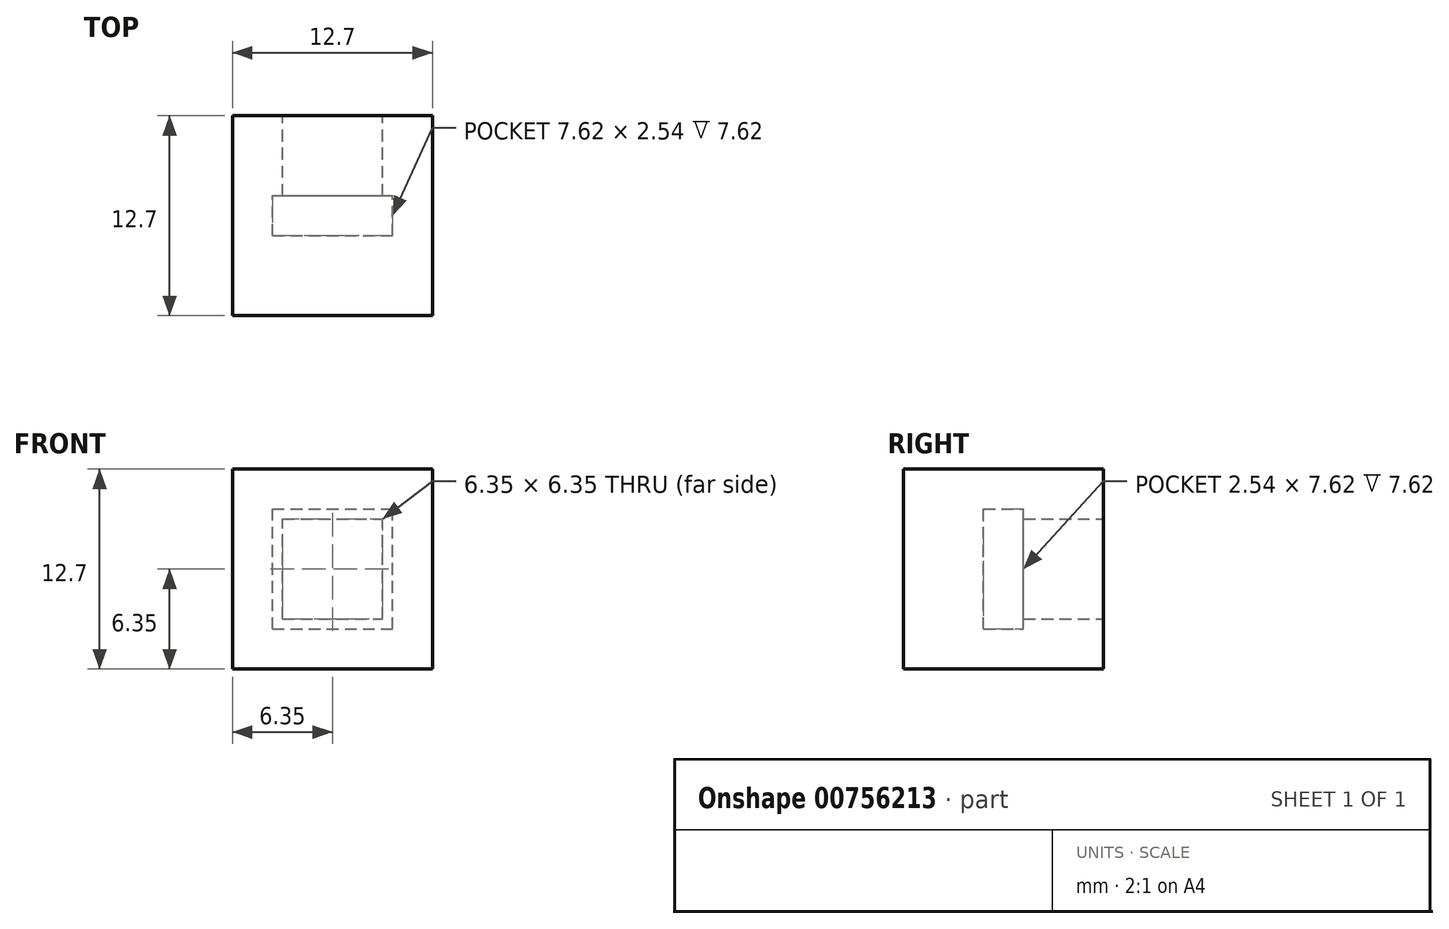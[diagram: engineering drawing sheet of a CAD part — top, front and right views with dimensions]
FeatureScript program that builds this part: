
annotation { "Feature Type Name" : "Feature", "Feature Type Description" : "" }
export const myFeature = defineFeature(function(context is Context, id is Id, definition is map)
    precondition{}
    {
        {
            var Q0;
            Q0=qCreatedBy(makeId("Front.planeOp"),FACE);
            var sketch = newSketch(context, id + "F0", { "sketchPlane" : qUnion([Q0])});
            skLineSegment(sketch, "E0.bottom", {"start": v(-6.35, -6.35) * mm, "end": v(6.35, -6.35) * mm});
            skLineSegment(sketch, "E0.top", {"start": v(-6.35, 6.35) * mm, "end": v(6.35, 6.35) * mm});
            skLineSegment(sketch, "E0.left", {"start": v(-6.35, -6.35) * mm, "end": v(-6.35, 6.35) * mm});
            skLineSegment(sketch, "E0.right", {"start": v(6.35, -6.35) * mm, "end": v(6.35, 6.35) * mm});
            skPoint(sketch, "E0.middle", {"position": v(0, 0) * mm});
            skLineSegment(sketch, "E1.bottom", {"start": v(-3.8, -3.81) * mm, "end": v(3.81, -3.81) * mm});
            skLineSegment(sketch, "E1.top", {"start": v(-3.81, 3.81) * mm, "end": v(3.8, 3.81) * mm});
            skLineSegment(sketch, "E1.left", {"start": v(-3.8, -3.81) * mm, "end": v(-3.81, 3.8) * mm});
            skLineSegment(sketch, "E1.right", {"start": v(3.81, -3.81) * mm, "end": v(3.8, 3.81) * mm});
            skLineSegment(sketch, "E2.bottom", {"start": v(-3.17, -3.18) * mm, "end": v(3.18, -3.18) * mm});
            skLineSegment(sketch, "E2.top", {"start": v(-3.18, 3.18) * mm, "end": v(3.17, 3.18) * mm});
            skLineSegment(sketch, "E2.left", {"start": v(-3.17, -3.18) * mm, "end": v(-3.18, 3.18) * mm});
            skLineSegment(sketch, "E2.right", {"start": v(3.18, -3.18) * mm, "end": v(3.17, 3.18) * mm});
            skSolve(sketch);
        }
        {
            var Q0;
            Q0 = qSketchRegion(id + "F0", true);
            var Q1;
            Q1=makeQuery(id+"F0.imprint","IMPRINT",FACE,{"disambiguationData":[TD([[makeQuery(id+"F0.imprint","IMPRINT",EDGE,{"derivedFrom":sQuery(id+"F0.wireOp",EDGE,"E1.bottom")}),1.0]])]});
            var Q2;
            Q2=makeQuery(id+"F0.imprint","IMPRINT",FACE,{"disambiguationData":[TD([[makeQuery(id+"F0.imprint","IMPRINT",EDGE,{"derivedFrom":sQuery(id+"F0.wireOp",EDGE,"E2.bottom")}),1.0]])]});
            extrude(context, id + "F1", {"entities" : qUnion([Q0, Q1, Q2]), "depth" : 12.7 * mm, "offsetDistance" : 25.4 * mm});
        }
        {
            var Q0;
            Q0=makeQuery(id+"F0.imprint","IMPRINT",FACE,{"disambiguationData":[TD([[makeQuery(id+"F0.imprint","IMPRINT",EDGE,{"derivedFrom":sQuery(id+"F0.wireOp",EDGE,"E2.bottom")}),1.0]])]});
            extrude(context, id + "F2", {"entities" : qUnion([Q0]), "operationType" : NewBodyOperationType.REMOVE, "depth" : 7.62 * mm, "offsetDistance" : 25.4 * mm});
        }
        {
            var Q0;
            Q0=makeQuery(id+"F0.imprint","IMPRINT",FACE,{"disambiguationData":[TD([[makeQuery(id+"F0.imprint","IMPRINT",EDGE,{"derivedFrom":sQuery(id+"F0.wireOp",EDGE,"E1.bottom")}),1.0]])]});
            extrude(context, id + "F3", {"entities" : qUnion([Q0]), "operationType" : NewBodyOperationType.REMOVE, "depth" : 7.62 * mm, "offsetDistance" : 25.4 * mm});
        }
        {
            var Q0;
            Q0=makeQuery(id+"F0.imprint","IMPRINT",FACE,{"disambiguationData":[TD([[makeQuery(id+"F0.imprint","IMPRINT",EDGE,{"derivedFrom":sQuery(id+"F0.wireOp",EDGE,"E1.bottom")}),1.0]])]});
            extrude(context, id + "F4", {"entities" : qUnion([Q0]), "operationType" : NewBodyOperationType.ADD, "depth" : 5.08 * mm, "offsetDistance" : 25.4 * mm});
        }
    });
